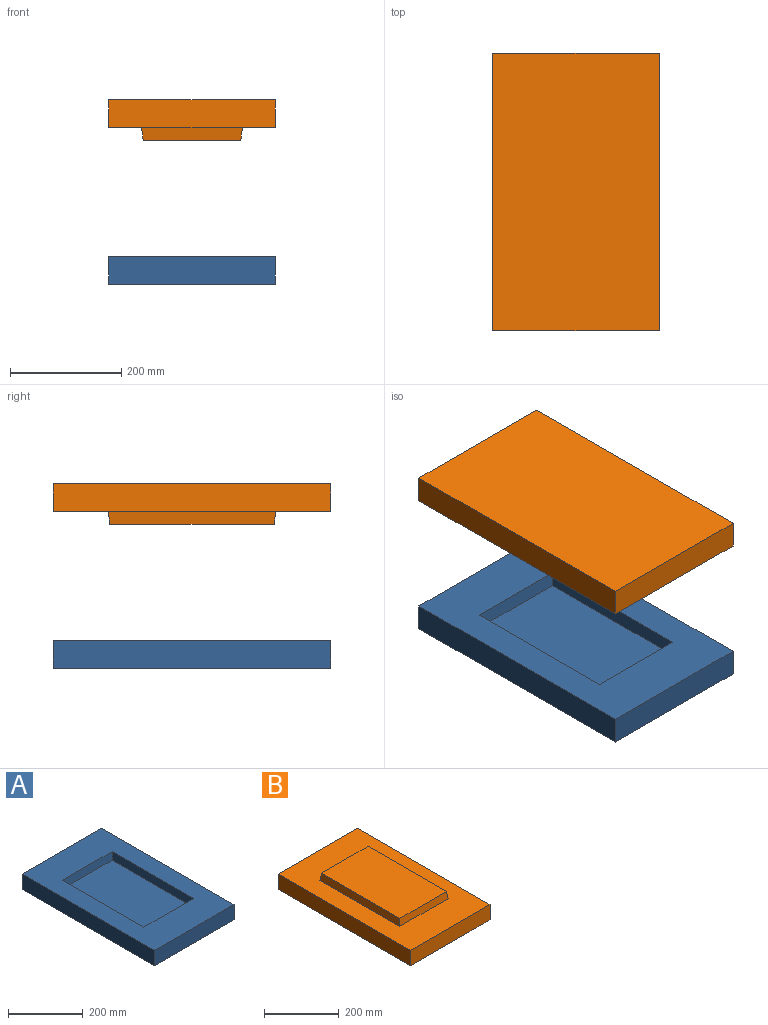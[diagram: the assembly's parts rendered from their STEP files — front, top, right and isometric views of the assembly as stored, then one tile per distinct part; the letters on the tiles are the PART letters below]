
ASSEMBLY  parts=2 mates=1
PART A: 11 faces, bbox 300x500x50 mm
  f0: plane 500x300mm, normal (0,0,1), area 92591mm2, adj f1,f2,f3,f4,f6,f7,f8,f9
  f1: plane 300x50mm, normal (0,-1,0), area 15000mm2, adj f0,f2,f4,f5
  f2: plane 500x50mm, normal (1,0,0), area 25000mm2, adj f0,f1,f3,f5
  f3: plane 300x50mm, normal (0,1,0), area 15000mm2, adj f0,f2,f4,f5
  f4: plane 500x50mm, normal (-1,0,0), area 25000mm2, adj f0,f1,f3,f5
  f5: plane 500x300mm, normal (0,0,-1), area 150000mm2, adj f1,f2,f3,f4
  f6: plane 187x25mm, normal (0,0.99,0.14), area 4632.2mm2, adj f0,f7,f9,f10
  f7: plane 307x25mm, normal (-0.99,0,0.14), area 7661.7mm2, adj f0,f6,f8,f10
  f8: plane 187x25mm, normal (0,-0.99,0.14), area 4632.2mm2, adj f0,f7,f9,f10
  f9: plane 307x25mm, normal (0.99,0,0.14), area 7661.7mm2, adj f0,f6,f8,f10
  f10: plane 299.97x179.97mm, normal (0,0,1), area 53987mm2, adj f6,f7,f8,f9
PART B: 11 faces, bbox 300x500x73 mm
  f0: plane 500x300mm, normal (0,0,1), area 95036mm2, adj f1,f2,f3,f4,f6,f7,f8,f9
  f1: plane 500x50mm, normal (-1,0,0), area 25000mm2, adj f0,f2,f4,f5
  f2: plane 300x50mm, normal (0,-1,0), area 15000mm2, adj f0,f1,f3,f5
  f3: plane 500x50mm, normal (1,0,0), area 25000mm2, adj f0,f2,f4,f5
  f4: plane 300x50mm, normal (0,1,0), area 15000mm2, adj f0,f1,f3,f5
  f5: plane 500x300mm, normal (0,0,-1), area 150000mm2, adj f1,f2,f3,f4
  f6: plane 182x23mm, normal (0,-0.99,0.14), area 4152.1mm2, adj f0,f7,f9,f10
  f7: plane 302x23mm, normal (0.99,0,0.14), area 6939.2mm2, adj f0,f6,f8,f10
  f8: plane 182x23mm, normal (0,0.99,0.14), area 4152.1mm2, adj f0,f7,f9,f10
  f9: plane 302x23mm, normal (-0.99,0,0.14), area 6939.2mm2, adj f0,f6,f8,f10
  f10: plane 295.54x175.54mm, normal (0,0,1), area 51876.8mm2, adj f6,f7,f8,f9
PLACE A t=(154.59,-106.23,0)mm
PLACE B rot(axis=(1,0,0),180deg) t=(154.59,-106.23,1532.24)mm
MATE slider B.f0 <-> A.f0  axis (0,0,-1) through (304.59,-356.23,1082.24)mm
